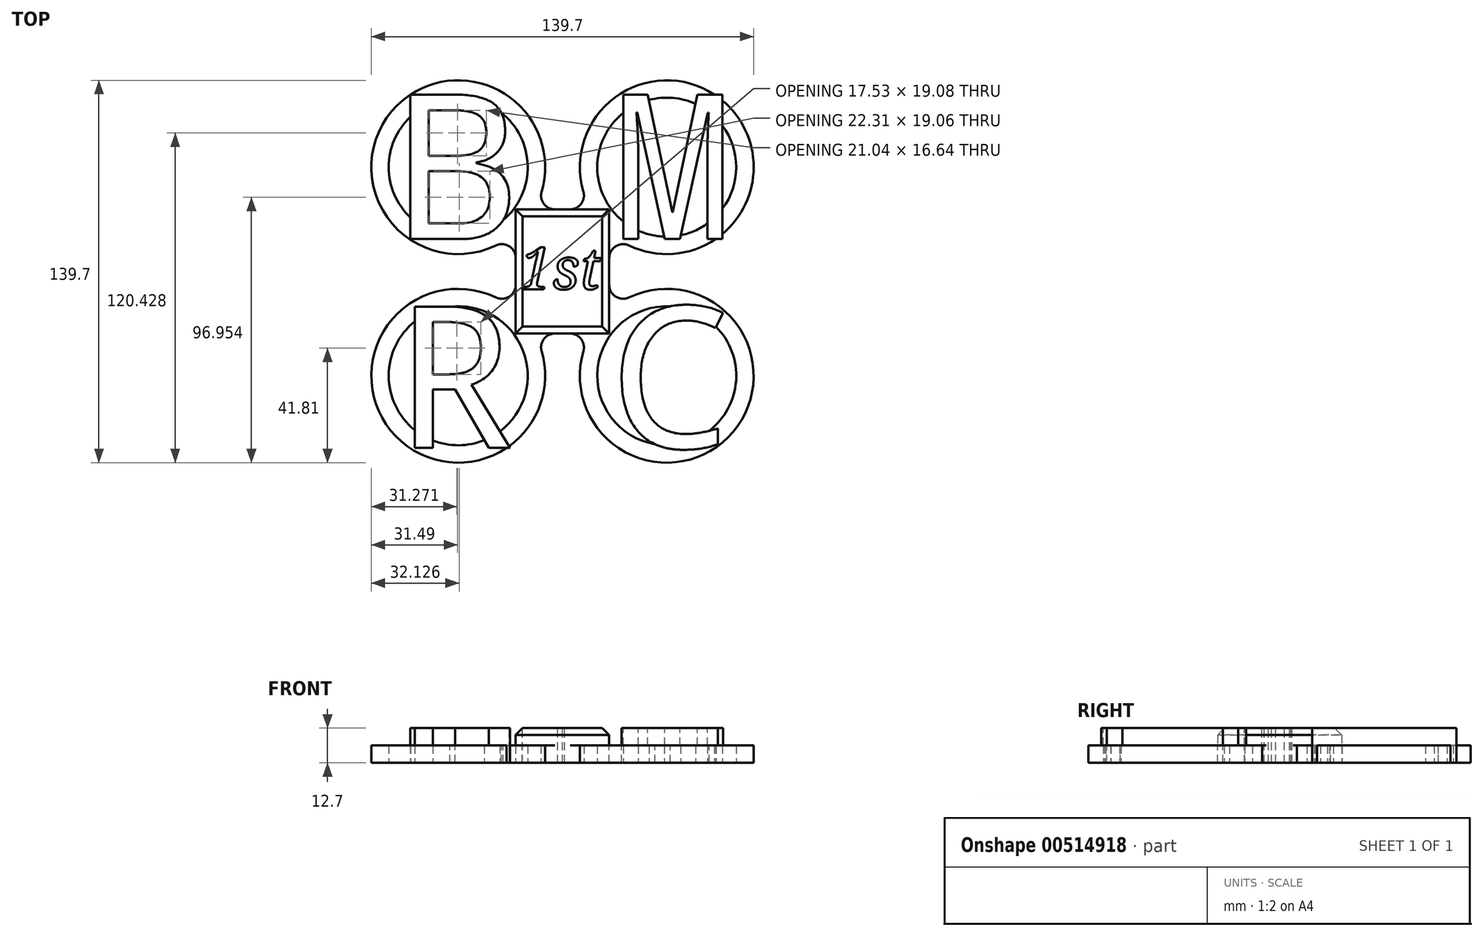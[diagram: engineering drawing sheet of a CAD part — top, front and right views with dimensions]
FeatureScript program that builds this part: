
annotation { "Feature Type Name" : "Feature", "Feature Type Description" : "" }
export const myFeature = defineFeature(function(context is Context, id is Id, definition is map)
    precondition{}
    {
        {
            var Q0;
            Q0=qCreatedBy(makeId("Top.planeOp"),FACE);
            var sketch = newSketch(context, id + "F0", { "sketchPlane" : qUnion([Q0])});
            skLineSegment(sketch, "E0.bottom", {"start": v(38.1, -38.1) * mm, "end": v(-38.1, -38.1) * mm, "construction": true});
            skLineSegment(sketch, "E0.top", {"start": v(38.1, 38.1) * mm, "end": v(-38.1, 38.1) * mm, "construction": true});
            skLineSegment(sketch, "E0.left", {"start": v(38.1, -38.1) * mm, "end": v(38.1, 38.1) * mm, "construction": true});
            skLineSegment(sketch, "E0.right", {"start": v(-38.1, -38.1) * mm, "end": v(-38.1, 38.1) * mm, "construction": true});
            skPoint(sketch, "E0.middle", {"position": v(0, 0) * mm});
            skCircle(sketch, "E1", {"center": v(-38.1, 38.1) * mm, "radius": 31.75 * mm});
            skCircle(sketch, "E2", {"center": v(-38.1, 38.1) * mm, "radius": 25.4 * mm});
            skCircle(sketch, "E3", {"center": v(38.1, 38.1) * mm, "radius": 31.75 * mm});
            skCircle(sketch, "E4", {"center": v(38.1, 38.1) * mm, "radius": 25.4 * mm});
            skCircle(sketch, "E5", {"center": v(-38.1, -38.1) * mm, "radius": 31.75 * mm});
            skCircle(sketch, "E6", {"center": v(-38.1, -38.1) * mm, "radius": 25.4 * mm});
            skCircle(sketch, "E7", {"center": v(38.1, -38.1) * mm, "radius": 31.75 * mm});
            skCircle(sketch, "E8", {"center": v(38.1, -38.1) * mm, "radius": 25.4 * mm});
            skSolve(sketch);
        }
        {
            var Q0;
            Q0=qSketchRegion(id+"F0",true);
            extrude(context, id + "F1", {"entities" : qUnion([Q0]), "depth" : 6.35 * mm, "offsetDistance" : 25.4 * mm});
        }
        {
            var Q0;
            Q0=qCreatedBy(makeId("Top.planeOp"),FACE);
            var sketch = newSketch(context, id + "F2", { "sketchPlane" : qUnion([Q0])});
            skLineSegment(sketch, "E9.bottom", {"start": v(-17.08, -22.68) * mm, "end": v(17.08, -22.68) * mm});
            skLineSegment(sketch, "E9.top", {"start": v(-17.08, 22.68) * mm, "end": v(17.08, 22.68) * mm});
            skLineSegment(sketch, "E9.left", {"start": v(-17.08, -22.68) * mm, "end": v(-17.08, 22.68) * mm});
            skLineSegment(sketch, "E9.right", {"start": v(17.08, -22.68) * mm, "end": v(17.08, 22.68) * mm});
            skPoint(sketch, "E9.middle", {"position": v(0, 0) * mm});
            skSolve(sketch);
        }
        {
            var Q0;
            Q0=qSketchRegion(id+"F2",true);
            extrude(context, id + "F3", {"entities" : qUnion([Q0]), "operationType" : NewBodyOperationType.ADD, "depth" : 12.7 * mm, "offsetDistance" : 25.4 * mm});
        }
        {
            var Q0;
            Q0=makeQuery(id+"F3.opExtrude","CAP_FACE",FACE,{"disambiguationData":[OSD([sQuery(id+"F2.wireOp",EDGE,"E9.bottom"),sQuery(id+"F2.wireOp",EDGE,"E9.top"),sQuery(id+"F2.wireOp",EDGE,"E9.left"),sQuery(id+"F2.wireOp",EDGE,"E9.right")])],"isStart":false});
            var sketch = newSketch(context, id + "F4", { "sketchPlane" : qUnion([Q0])});
            skText(sketch, "E10", { "text": "B", "fontName": "DroidSansMono.ttf"});
            skText(sketch, "E11", { "text": "M", "fontName": "DroidSansMono.ttf"});
            skText(sketch, "E12", { "text": "R", "fontName": "DroidSansMono.ttf"});
            skText(sketch, "E13", { "text": "C", "fontName": "DroidSansMono.ttf"});
            const initialGuessF4  = {"E10": [-0.0605, 0.01187, 1, 0, 0.05322], "E11": [0.01816, 0.01187, 1, 0, 0.05322], "E12": [-0.0605, -0.06445, 1, 0, 0.052], "E13": [0.01708, -0.06445, 1, 0, 0.052]};
            skSetInitialGuess(sketch, initialGuessF4);
            skSolve(sketch);
        }
        {
            var Q0;
            Q0=qSketchRegion(id+"F4",true);
            var Q1;
            Q1=makeQuery(id+"F3.boolean.opBoolean","MERGE",FACE,{"derivedFrom":[makeQuery(id+"F1.opExtrude","CAP_FACE",FACE,{"disambiguationData":[OSD([sQuery(id+"F0.wireOp",EDGE,"E1"),sQuery(id+"F0.wireOp",EDGE,"E2")])],"isStart":true}),makeQuery(id+"F1.opExtrude","CAP_FACE",FACE,{"disambiguationData":[OSD([sQuery(id+"F0.wireOp",EDGE,"E3"),sQuery(id+"F0.wireOp",EDGE,"E4")])],"isStart":true}),makeQuery(id+"F1.opExtrude","CAP_FACE",FACE,{"disambiguationData":[OSD([sQuery(id+"F0.wireOp",EDGE,"E5"),sQuery(id+"F0.wireOp",EDGE,"E6")])],"isStart":true}),makeQuery(id+"F1.opExtrude","CAP_FACE",FACE,{"disambiguationData":[OSD([sQuery(id+"F0.wireOp",EDGE,"E7"),sQuery(id+"F0.wireOp",EDGE,"E8")])],"isStart":true}),makeQuery(id+"F3.opExtrude","CAP_FACE",FACE,{"disambiguationData":[OSD([sQuery(id+"F2.wireOp",EDGE,"E9.bottom"),sQuery(id+"F2.wireOp",EDGE,"E9.top"),sQuery(id+"F2.wireOp",EDGE,"E9.left"),sQuery(id+"F2.wireOp",EDGE,"E9.right")])],"isStart":true})]});
            extrude(context, id + "F5", {"entities" : qUnion([Q0]), "operationType" : NewBodyOperationType.ADD, "endBound" : BoundingType.UP_TO_SURFACE, "oppositeDirection" : true, "depth" : 25.4 * mm, "endBoundEntityFace" : qUnion([Q1]), "offsetDistance" : 25.4 * mm});
        }
        {
            var Q0;
            Q0=makeQuery(id+"F3.opExtrude","CAP_FACE",FACE,{"disambiguationData":[OSD([sQuery(id+"F2.wireOp",EDGE,"E9.bottom"),sQuery(id+"F2.wireOp",EDGE,"E9.top"),sQuery(id+"F2.wireOp",EDGE,"E9.left"),sQuery(id+"F2.wireOp",EDGE,"E9.right")])],"isStart":false});
            var sketch = newSketch(context, id + "F6", { "sketchPlane" : qUnion([Q0])});
            skText(sketch, "E14", { "text": "1st", "fontName": "NotoSerif-Italic.ttf"});
            const initialGuessF6  = {"E14": [-0.01557, -0.00649, 1, 0, 0.01534]};
            skSetInitialGuess(sketch, initialGuessF6);
            skSolve(sketch);
        }
        {
            var Q0;
            Q0=qSketchRegion(id+"F6",true);
            extrude(context, id + "F7", {"entities" : qUnion([Q0]), "operationType" : NewBodyOperationType.REMOVE, "oppositeDirection" : true, "depth" : 25.4 * mm, "offsetDistance" : 25.4 * mm});
        }
        {
            var Q0;
            Q0=makeQuery(id+"F3.boolean.opBoolean","INTERSECT",EDGE,{"derivedFrom":[makeQuery(id+"F1.opExtrude","SWEPT_FACE",FACE,{"disambiguationData":[OSD([sQuery(id+"F0.wireOp",EDGE,"E7")])]}),makeQuery(id+"F3.opExtrude","SWEPT_FACE",FACE,{"disambiguationData":[OSD([sQuery(id+"F2.wireOp",EDGE,"E9.right")])]})]});
            var Q1;
            Q1=makeQuery(id+"F3.boolean.opBoolean","INTERSECT",EDGE,{"derivedFrom":[makeQuery(id+"F1.opExtrude","SWEPT_FACE",FACE,{"disambiguationData":[OSD([sQuery(id+"F0.wireOp",EDGE,"E1")])]}),makeQuery(id+"F3.opExtrude","SWEPT_FACE",FACE,{"disambiguationData":[OSD([sQuery(id+"F2.wireOp",EDGE,"E9.left")])]})]});
            var Q2;
            Q2=makeQuery(id+"F3.boolean.opBoolean","INTERSECT",EDGE,{"derivedFrom":[makeQuery(id+"F1.opExtrude","SWEPT_FACE",FACE,{"disambiguationData":[OSD([sQuery(id+"F0.wireOp",EDGE,"E3")])]}),makeQuery(id+"F3.opExtrude","SWEPT_FACE",FACE,{"disambiguationData":[OSD([sQuery(id+"F2.wireOp",EDGE,"E9.right")])]})]});
            var Q3;
            Q3=makeQuery(id+"F3.boolean.opBoolean","INTERSECT",EDGE,{"derivedFrom":[makeQuery(id+"F1.opExtrude","SWEPT_FACE",FACE,{"disambiguationData":[OSD([sQuery(id+"F0.wireOp",EDGE,"E7")])]}),makeQuery(id+"F3.opExtrude","SWEPT_FACE",FACE,{"disambiguationData":[OSD([sQuery(id+"F2.wireOp",EDGE,"E9.bottom")])]})]});
            var Q4;
            Q4=makeQuery(id+"F3.boolean.opBoolean","INTERSECT",EDGE,{"derivedFrom":[makeQuery(id+"F1.opExtrude","SWEPT_FACE",FACE,{"disambiguationData":[OSD([sQuery(id+"F0.wireOp",EDGE,"E5")])]}),makeQuery(id+"F3.opExtrude","SWEPT_FACE",FACE,{"disambiguationData":[OSD([sQuery(id+"F2.wireOp",EDGE,"E9.bottom")])]})]});
            var Q5;
            Q5=makeQuery(id+"F3.boolean.opBoolean","INTERSECT",EDGE,{"derivedFrom":[makeQuery(id+"F1.opExtrude","SWEPT_FACE",FACE,{"disambiguationData":[OSD([sQuery(id+"F0.wireOp",EDGE,"E1")])]}),makeQuery(id+"F3.opExtrude","SWEPT_FACE",FACE,{"disambiguationData":[OSD([sQuery(id+"F2.wireOp",EDGE,"E9.top")])]})]});
            var Q6;
            Q6=makeQuery(id+"F3.boolean.opBoolean","INTERSECT",EDGE,{"derivedFrom":[makeQuery(id+"F1.opExtrude","SWEPT_FACE",FACE,{"disambiguationData":[OSD([sQuery(id+"F0.wireOp",EDGE,"E3")])]}),makeQuery(id+"F3.opExtrude","SWEPT_FACE",FACE,{"disambiguationData":[OSD([sQuery(id+"F2.wireOp",EDGE,"E9.top")])]})]});
            var Q7;
            Q7=makeQuery(id+"F3.boolean.opBoolean","INTERSECT",EDGE,{"derivedFrom":[makeQuery(id+"F1.opExtrude","SWEPT_FACE",FACE,{"disambiguationData":[OSD([sQuery(id+"F0.wireOp",EDGE,"E5")])]}),makeQuery(id+"F3.opExtrude","SWEPT_FACE",FACE,{"disambiguationData":[OSD([sQuery(id+"F2.wireOp",EDGE,"E9.left")])]})]});
            fillet(context, id + "F8", {"entities" : qUnion([Q0, Q1, Q2, Q3, Q4, Q5, Q6, Q7]), "radius" : 5.08 * mm, "tangentPropagation" : true, "allowEdgeOverflow" : false});
        }
        {
            var Q0;
            Q0=makeQuery(id+"F3.opExtrude","CAP_EDGE",EDGE,{"disambiguationData":[OSD([sQuery(id+"F2.wireOp",EDGE,"E9.left")])],"isStart":false});
            var Q1;
            Q1=makeQuery(id+"F3.opExtrude","CAP_EDGE",EDGE,{"disambiguationData":[OSD([sQuery(id+"F2.wireOp",EDGE,"E9.bottom")])],"isStart":false});
            var Q2;
            Q2=makeQuery(id+"F3.opExtrude","CAP_EDGE",EDGE,{"disambiguationData":[OSD([sQuery(id+"F2.wireOp",EDGE,"E9.right")])],"isStart":false});
            var Q3;
            Q3=makeQuery(id+"F3.opExtrude","CAP_EDGE",EDGE,{"disambiguationData":[OSD([sQuery(id+"F2.wireOp",EDGE,"E9.top")])],"isStart":false});
            chamfer(context, id + "F9", {"entities" : qUnion([Q0, Q1, Q2, Q3]), "width" : 2.54 * mm, "tangentPropagation" : true});
        }
    });
